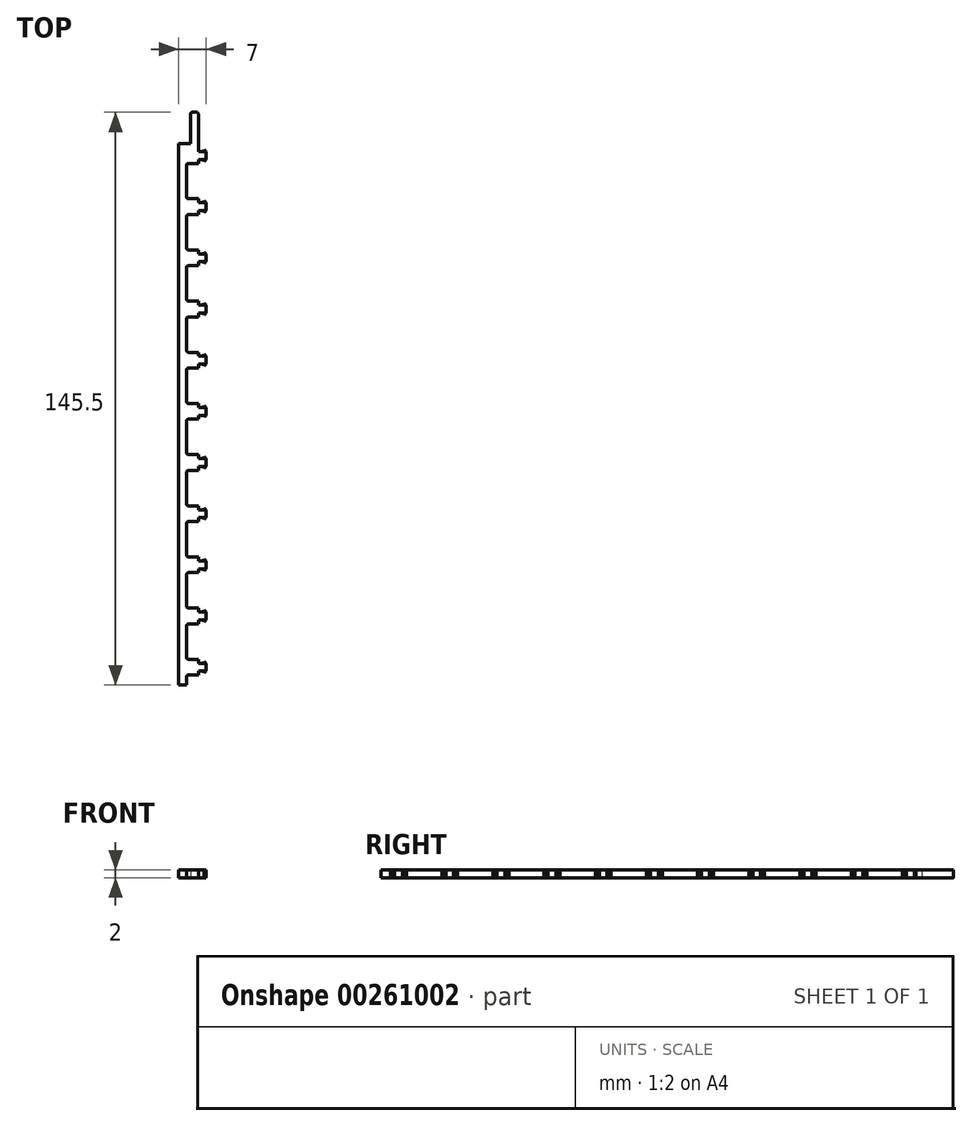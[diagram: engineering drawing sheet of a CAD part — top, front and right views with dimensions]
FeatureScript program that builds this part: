
annotation { "Feature Type Name" : "Feature", "Feature Type Description" : "" }
export const myFeature = defineFeature(function(context is Context, id is Id, definition is map)
    precondition{}
    {
        {
            var Q0;
            Q0=qCreatedBy(makeId("Top.planeOp"),FACE);
            var sketch = newSketch(context, id + "F0", { "sketchPlane" : qUnion([Q0])});
            skLineSegment(sketch, "E0.bottom", {"start": v(-167, 137.5) * mm, "end": v(167, 137.5) * mm});
            skLineSegment(sketch, "E0.top", {"start": v(-167, -137.5) * mm, "end": v(167, -137.5) * mm});
            skLineSegment(sketch, "E0.left", {"start": v(-167, 137.5) * mm, "end": v(-167, -137.5) * mm});
            skLineSegment(sketch, "E0.right", {"start": v(167, 137.5) * mm, "end": v(167, -137.5) * mm});
            skPoint(sketch, "E0.middle", {"position": v(0, 0) * mm});
            skLineSegment(sketch, "E1", {"start": v(-167, 137.5) * mm, "end": v(-172, 137.5) * mm});
            skLineSegment(sketch, "E2", {"start": v(-172, 137.5) * mm, "end": v(-172, -137.5) * mm});
            skLineSegment(sketch, "E3", {"start": v(-172, -137.5) * mm, "end": v(-167, -137.5) * mm});
            skLineSegment(sketch, "E4", {"start": v(-167, 132.5) * mm, "end": v(-169.5, 132.5) * mm});
            skLineSegment(sketch, "E5", {"start": v(-170, 132) * mm, "end": v(-170, 124) * mm});
            skLineSegment(sketch, "E6", {"start": v(-169.5, 123.5) * mm, "end": v(-167, 123.5) * mm});
            skLineSegment(sketch, "E7", {"start": v(-169, 137.5) * mm, "end": v(-169, 145) * mm});
            skLineSegment(sketch, "E8", {"start": v(-168.5, 145.5) * mm, "end": v(-167.5, 145.5) * mm});
            skLineSegment(sketch, "E9", {"start": v(-167, 145) * mm, "end": v(-167, 137.5) * mm});
            skPoint(sketch, "E10.visualSharp", {"position": v(-169, 145.5) * mm});
            skArc(sketch, "E10.filletArc", {"start": v(-168.5, 145.5) * mm, "mid": v(-168.85, 145.35) * mm, "end": v(-169, 145) * mm});
            skPoint(sketch, "E11.visualSharp", {"position": v(-167, 145.5) * mm});
            skArc(sketch, "E11.filletArc", {"start": v(-167, 145) * mm, "mid": v(-167.15, 145.35) * mm, "end": v(-167.5, 145.5) * mm});
            skLineSegment(sketch, "E12", {"start": v(-167, 135.5) * mm, "end": v(-165.5, 135.5) * mm});
            skLineSegment(sketch, "E13", {"start": v(-165.5, 135.5) * mm, "end": v(-165.5, 136) * mm});
            skLineSegment(sketch, "E14", {"start": v(-165.5, 136) * mm, "end": v(-165, 135.5) * mm});
            skLineSegment(sketch, "E15", {"start": v(-167, 134.5) * mm, "end": v(-162.16, 134.5) * mm, "construction": true});
            skLineSegment(sketch, "E16.MirrorCS", {"start": v(-167, 133.5) * mm, "end": v(-165.5, 133.5) * mm});
            skLineSegment(sketch, "E17.MirrorCS", {"start": v(-165.5, 133.5) * mm, "end": v(-165.5, 133) * mm});
            skLineSegment(sketch, "E18.MirrorCS", {"start": v(-165.5, 133) * mm, "end": v(-165, 133.5) * mm});
            skLineSegment(sketch, "E19", {"start": v(-165, 135.5) * mm, "end": v(-165, 133.5) * mm});
            skPoint(sketch, "E20.visualSharp", {"position": v(-170, 132.5) * mm});
            skArc(sketch, "E20.filletArc", {"start": v(-169.5, 132.5) * mm, "mid": v(-169.85, 132.35) * mm, "end": v(-170, 132) * mm});
            skPoint(sketch, "E21.visualSharp", {"position": v(-170, 123.5) * mm});
            skArc(sketch, "E21.filletArc", {"start": v(-170, 124) * mm, "mid": v(-169.85, 123.65) * mm, "end": v(-169.5, 123.5) * mm});
            skLineSegment(sketch, "E22.0.1.0", {"start": v(-167, 120.5) * mm, "end": v(-165.5, 120.5) * mm});
            skLineSegment(sketch, "E22.0.1.1", {"start": v(-165.5, 120.5) * mm, "end": v(-165.5, 120) * mm});
            skLineSegment(sketch, "E22.0.1.2", {"start": v(-165.5, 120) * mm, "end": v(-165, 120.5) * mm});
            skLineSegment(sketch, "E22.0.1.3", {"start": v(-165, 122.5) * mm, "end": v(-165, 120.5) * mm});
            skLineSegment(sketch, "E22.0.1.4", {"start": v(-165.5, 123) * mm, "end": v(-165, 122.5) * mm});
            skLineSegment(sketch, "E22.0.1.5", {"start": v(-165.5, 122.5) * mm, "end": v(-165.5, 123) * mm});
            skLineSegment(sketch, "E22.0.1.6", {"start": v(-167, 122.5) * mm, "end": v(-165.5, 122.5) * mm});
            skLineSegment(sketch, "E22.0.1.7", {"start": v(-167, 119.5) * mm, "end": v(-169.5, 119.5) * mm});
            skArc(sketch, "E22.0.1.8", {"start": v(-169.5, 119.5) * mm, "mid": v(-169.85, 119.35) * mm, "end": v(-170, 119) * mm});
            skLineSegment(sketch, "E22.0.1.9", {"start": v(-170, 119) * mm, "end": v(-170, 111) * mm});
            skArc(sketch, "E22.0.1.10", {"start": v(-170, 111) * mm, "mid": v(-169.85, 110.65) * mm, "end": v(-169.5, 110.5) * mm});
            skLineSegment(sketch, "E22.0.1.11", {"start": v(-169.5, 110.5) * mm, "end": v(-167, 110.5) * mm});
            skLineSegment(sketch, "E22.0.2.0", {"start": v(-167, 107.5) * mm, "end": v(-165.5, 107.5) * mm});
            skLineSegment(sketch, "E22.0.2.1", {"start": v(-165.5, 107.5) * mm, "end": v(-165.5, 107) * mm});
            skLineSegment(sketch, "E22.0.2.2", {"start": v(-165.5, 107) * mm, "end": v(-165, 107.5) * mm});
            skLineSegment(sketch, "E22.0.2.3", {"start": v(-165, 109.5) * mm, "end": v(-165, 107.5) * mm});
            skLineSegment(sketch, "E22.0.2.4", {"start": v(-165.5, 110) * mm, "end": v(-165, 109.5) * mm});
            skLineSegment(sketch, "E22.0.2.5", {"start": v(-165.5, 109.5) * mm, "end": v(-165.5, 110) * mm});
            skLineSegment(sketch, "E22.0.2.6", {"start": v(-167, 109.5) * mm, "end": v(-165.5, 109.5) * mm});
            skLineSegment(sketch, "E22.0.2.7", {"start": v(-167, 106.5) * mm, "end": v(-169.5, 106.5) * mm});
            skArc(sketch, "E22.0.2.8", {"start": v(-169.5, 106.5) * mm, "mid": v(-169.85, 106.35) * mm, "end": v(-170, 106) * mm});
            skLineSegment(sketch, "E22.0.2.9", {"start": v(-170, 106) * mm, "end": v(-170, 98) * mm});
            skArc(sketch, "E22.0.2.10", {"start": v(-170, 98) * mm, "mid": v(-169.85, 97.65) * mm, "end": v(-169.5, 97.5) * mm});
            skLineSegment(sketch, "E22.0.2.11", {"start": v(-169.5, 97.5) * mm, "end": v(-167, 97.5) * mm});
            skLineSegment(sketch, "E22.0.3.0", {"start": v(-167, 94.5) * mm, "end": v(-165.5, 94.5) * mm});
            skLineSegment(sketch, "E22.0.3.1", {"start": v(-165.5, 94.5) * mm, "end": v(-165.5, 94) * mm});
            skLineSegment(sketch, "E22.0.3.2", {"start": v(-165.5, 94) * mm, "end": v(-165, 94.5) * mm});
            skLineSegment(sketch, "E22.0.3.3", {"start": v(-165, 96.5) * mm, "end": v(-165, 94.5) * mm});
            skLineSegment(sketch, "E22.0.3.4", {"start": v(-165.5, 97) * mm, "end": v(-165, 96.5) * mm});
            skLineSegment(sketch, "E22.0.3.5", {"start": v(-165.5, 96.5) * mm, "end": v(-165.5, 97) * mm});
            skLineSegment(sketch, "E22.0.3.6", {"start": v(-167, 96.5) * mm, "end": v(-165.5, 96.5) * mm});
            skLineSegment(sketch, "E22.0.3.7", {"start": v(-167, 93.5) * mm, "end": v(-169.5, 93.5) * mm});
            skArc(sketch, "E22.0.3.8", {"start": v(-169.5, 93.5) * mm, "mid": v(-169.85, 93.35) * mm, "end": v(-170, 93) * mm});
            skLineSegment(sketch, "E22.0.3.9", {"start": v(-170, 93) * mm, "end": v(-170, 85) * mm});
            skArc(sketch, "E22.0.3.10", {"start": v(-170, 85) * mm, "mid": v(-169.85, 84.65) * mm, "end": v(-169.5, 84.5) * mm});
            skLineSegment(sketch, "E22.0.3.11", {"start": v(-169.5, 84.5) * mm, "end": v(-167, 84.5) * mm});
            skLineSegment(sketch, "E22.0.4.0", {"start": v(-167, 81.5) * mm, "end": v(-165.5, 81.5) * mm});
            skLineSegment(sketch, "E22.0.4.1", {"start": v(-165.5, 81.5) * mm, "end": v(-165.5, 81) * mm});
            skLineSegment(sketch, "E22.0.4.2", {"start": v(-165.5, 81) * mm, "end": v(-165, 81.5) * mm});
            skLineSegment(sketch, "E22.0.4.3", {"start": v(-165, 83.5) * mm, "end": v(-165, 81.5) * mm});
            skLineSegment(sketch, "E22.0.4.4", {"start": v(-165.5, 84) * mm, "end": v(-165, 83.5) * mm});
            skLineSegment(sketch, "E22.0.4.5", {"start": v(-165.5, 83.5) * mm, "end": v(-165.5, 84) * mm});
            skLineSegment(sketch, "E22.0.4.6", {"start": v(-167, 83.5) * mm, "end": v(-165.5, 83.5) * mm});
            skLineSegment(sketch, "E22.0.4.7", {"start": v(-167, 80.5) * mm, "end": v(-169.5, 80.5) * mm});
            skArc(sketch, "E22.0.4.8", {"start": v(-169.5, 80.5) * mm, "mid": v(-169.85, 80.35) * mm, "end": v(-170, 80) * mm});
            skLineSegment(sketch, "E22.0.4.9", {"start": v(-170, 80) * mm, "end": v(-170, 72) * mm});
            skArc(sketch, "E22.0.4.10", {"start": v(-170, 72) * mm, "mid": v(-169.85, 71.65) * mm, "end": v(-169.5, 71.5) * mm});
            skLineSegment(sketch, "E22.0.4.11", {"start": v(-169.5, 71.5) * mm, "end": v(-167, 71.5) * mm});
            skLineSegment(sketch, "E22.0.5.0", {"start": v(-167, 68.5) * mm, "end": v(-165.5, 68.5) * mm});
            skLineSegment(sketch, "E22.0.5.1", {"start": v(-165.5, 68.5) * mm, "end": v(-165.5, 68) * mm});
            skLineSegment(sketch, "E22.0.5.2", {"start": v(-165.5, 68) * mm, "end": v(-165, 68.5) * mm});
            skLineSegment(sketch, "E22.0.5.3", {"start": v(-165, 70.5) * mm, "end": v(-165, 68.5) * mm});
            skLineSegment(sketch, "E22.0.5.4", {"start": v(-165.5, 71) * mm, "end": v(-165, 70.5) * mm});
            skLineSegment(sketch, "E22.0.5.5", {"start": v(-165.5, 70.5) * mm, "end": v(-165.5, 71) * mm});
            skLineSegment(sketch, "E22.0.5.6", {"start": v(-167, 70.5) * mm, "end": v(-165.5, 70.5) * mm});
            skLineSegment(sketch, "E22.0.5.7", {"start": v(-167, 67.5) * mm, "end": v(-169.5, 67.5) * mm});
            skArc(sketch, "E22.0.5.8", {"start": v(-169.5, 67.5) * mm, "mid": v(-169.85, 67.35) * mm, "end": v(-170, 67) * mm});
            skLineSegment(sketch, "E22.0.5.9", {"start": v(-170, 67) * mm, "end": v(-170, 59) * mm});
            skArc(sketch, "E22.0.5.10", {"start": v(-170, 59) * mm, "mid": v(-169.85, 58.65) * mm, "end": v(-169.5, 58.5) * mm});
            skLineSegment(sketch, "E22.0.5.11", {"start": v(-169.5, 58.5) * mm, "end": v(-167, 58.5) * mm});
            skLineSegment(sketch, "E22.0.6.0", {"start": v(-167, 55.5) * mm, "end": v(-165.5, 55.5) * mm});
            skLineSegment(sketch, "E22.0.6.1", {"start": v(-165.5, 55.5) * mm, "end": v(-165.5, 55) * mm});
            skLineSegment(sketch, "E22.0.6.2", {"start": v(-165.5, 55) * mm, "end": v(-165, 55.5) * mm});
            skLineSegment(sketch, "E22.0.6.3", {"start": v(-165, 57.5) * mm, "end": v(-165, 55.5) * mm});
            skLineSegment(sketch, "E22.0.6.4", {"start": v(-165.5, 58) * mm, "end": v(-165, 57.5) * mm});
            skLineSegment(sketch, "E22.0.6.5", {"start": v(-165.5, 57.5) * mm, "end": v(-165.5, 58) * mm});
            skLineSegment(sketch, "E22.0.6.6", {"start": v(-167, 57.5) * mm, "end": v(-165.5, 57.5) * mm});
            skLineSegment(sketch, "E22.0.6.7", {"start": v(-167, 54.5) * mm, "end": v(-169.5, 54.5) * mm});
            skArc(sketch, "E22.0.6.8", {"start": v(-169.5, 54.5) * mm, "mid": v(-169.85, 54.35) * mm, "end": v(-170, 54) * mm});
            skLineSegment(sketch, "E22.0.6.9", {"start": v(-170, 54) * mm, "end": v(-170, 46) * mm});
            skArc(sketch, "E22.0.6.10", {"start": v(-170, 46) * mm, "mid": v(-169.85, 45.65) * mm, "end": v(-169.5, 45.5) * mm});
            skLineSegment(sketch, "E22.0.6.11", {"start": v(-169.5, 45.5) * mm, "end": v(-167, 45.5) * mm});
            skLineSegment(sketch, "E22.0.7.0", {"start": v(-167, 42.5) * mm, "end": v(-165.5, 42.5) * mm});
            skLineSegment(sketch, "E22.0.7.1", {"start": v(-165.5, 42.5) * mm, "end": v(-165.5, 42) * mm});
            skLineSegment(sketch, "E22.0.7.2", {"start": v(-165.5, 42) * mm, "end": v(-165, 42.5) * mm});
            skLineSegment(sketch, "E22.0.7.3", {"start": v(-165, 44.5) * mm, "end": v(-165, 42.5) * mm});
            skLineSegment(sketch, "E22.0.7.4", {"start": v(-165.5, 45) * mm, "end": v(-165, 44.5) * mm});
            skLineSegment(sketch, "E22.0.7.5", {"start": v(-165.5, 44.5) * mm, "end": v(-165.5, 45) * mm});
            skLineSegment(sketch, "E22.0.7.6", {"start": v(-167, 44.5) * mm, "end": v(-165.5, 44.5) * mm});
            skLineSegment(sketch, "E22.0.7.7", {"start": v(-167, 41.5) * mm, "end": v(-169.5, 41.5) * mm});
            skArc(sketch, "E22.0.7.8", {"start": v(-169.5, 41.5) * mm, "mid": v(-169.85, 41.35) * mm, "end": v(-170, 41) * mm});
            skLineSegment(sketch, "E22.0.7.9", {"start": v(-170, 41) * mm, "end": v(-170, 33) * mm});
            skArc(sketch, "E22.0.7.10", {"start": v(-170, 33) * mm, "mid": v(-169.85, 32.65) * mm, "end": v(-169.5, 32.5) * mm});
            skLineSegment(sketch, "E22.0.7.11", {"start": v(-169.5, 32.5) * mm, "end": v(-167, 32.5) * mm});
            skLineSegment(sketch, "E22.0.8.0", {"start": v(-167, 29.5) * mm, "end": v(-165.5, 29.5) * mm});
            skLineSegment(sketch, "E22.0.8.1", {"start": v(-165.5, 29.5) * mm, "end": v(-165.5, 29) * mm});
            skLineSegment(sketch, "E22.0.8.2", {"start": v(-165.5, 29) * mm, "end": v(-165, 29.5) * mm});
            skLineSegment(sketch, "E22.0.8.3", {"start": v(-165, 31.5) * mm, "end": v(-165, 29.5) * mm});
            skLineSegment(sketch, "E22.0.8.4", {"start": v(-165.5, 32) * mm, "end": v(-165, 31.5) * mm});
            skLineSegment(sketch, "E22.0.8.5", {"start": v(-165.5, 31.5) * mm, "end": v(-165.5, 32) * mm});
            skLineSegment(sketch, "E22.0.8.6", {"start": v(-167, 31.5) * mm, "end": v(-165.5, 31.5) * mm});
            skLineSegment(sketch, "E22.0.8.7", {"start": v(-167, 28.5) * mm, "end": v(-169.5, 28.5) * mm});
            skArc(sketch, "E22.0.8.8", {"start": v(-169.5, 28.5) * mm, "mid": v(-169.85, 28.35) * mm, "end": v(-170, 28) * mm});
            skLineSegment(sketch, "E22.0.8.9", {"start": v(-170, 28) * mm, "end": v(-170, 20) * mm});
            skArc(sketch, "E22.0.8.10", {"start": v(-170, 20) * mm, "mid": v(-169.85, 19.65) * mm, "end": v(-169.5, 19.5) * mm});
            skLineSegment(sketch, "E22.0.8.11", {"start": v(-169.5, 19.5) * mm, "end": v(-167, 19.5) * mm});
            skLineSegment(sketch, "E22.0.9.0", {"start": v(-167, 16.5) * mm, "end": v(-165.5, 16.5) * mm});
            skLineSegment(sketch, "E22.0.9.1", {"start": v(-165.5, 16.5) * mm, "end": v(-165.5, 16) * mm});
            skLineSegment(sketch, "E22.0.9.2", {"start": v(-165.5, 16) * mm, "end": v(-165, 16.5) * mm});
            skLineSegment(sketch, "E22.0.9.3", {"start": v(-165, 18.5) * mm, "end": v(-165, 16.5) * mm});
            skLineSegment(sketch, "E22.0.9.4", {"start": v(-165.5, 19) * mm, "end": v(-165, 18.5) * mm});
            skLineSegment(sketch, "E22.0.9.5", {"start": v(-165.5, 18.5) * mm, "end": v(-165.5, 19) * mm});
            skLineSegment(sketch, "E22.0.9.6", {"start": v(-167, 18.5) * mm, "end": v(-165.5, 18.5) * mm});
            skLineSegment(sketch, "E22.0.9.7", {"start": v(-167, 15.5) * mm, "end": v(-169.5, 15.5) * mm});
            skArc(sketch, "E22.0.9.8", {"start": v(-169.5, 15.5) * mm, "mid": v(-169.85, 15.35) * mm, "end": v(-170, 15) * mm});
            skLineSegment(sketch, "E22.0.9.9", {"start": v(-170, 15) * mm, "end": v(-170, 7) * mm});
            skArc(sketch, "E22.0.9.10", {"start": v(-170, 7) * mm, "mid": v(-169.85, 6.65) * mm, "end": v(-169.5, 6.5) * mm});
            skLineSegment(sketch, "E22.0.9.11", {"start": v(-169.5, 6.5) * mm, "end": v(-167, 6.5) * mm});
            skLineSegment(sketch, "E22.0.10.0", {"start": v(-167, 3.5) * mm, "end": v(-165.5, 3.5) * mm});
            skLineSegment(sketch, "E22.0.10.1", {"start": v(-165.5, 3.5) * mm, "end": v(-165.5, 3) * mm});
            skLineSegment(sketch, "E22.0.10.2", {"start": v(-165.5, 3) * mm, "end": v(-165, 3.5) * mm});
            skLineSegment(sketch, "E22.0.10.3", {"start": v(-165, 5.5) * mm, "end": v(-165, 3.5) * mm});
            skLineSegment(sketch, "E22.0.10.4", {"start": v(-165.5, 6) * mm, "end": v(-165, 5.5) * mm});
            skLineSegment(sketch, "E22.0.10.5", {"start": v(-165.5, 5.5) * mm, "end": v(-165.5, 6) * mm});
            skLineSegment(sketch, "E22.0.10.6", {"start": v(-167, 5.5) * mm, "end": v(-165.5, 5.5) * mm});
            skLineSegment(sketch, "E22.0.10.7", {"start": v(-167, 2.5) * mm, "end": v(-169.5, 2.5) * mm});
            skArc(sketch, "E22.0.10.8", {"start": v(-169.5, 2.5) * mm, "mid": v(-169.85, 2.35) * mm, "end": v(-170, 2) * mm});
            skLineSegment(sketch, "E22.0.10.9", {"start": v(-170, 2) * mm, "end": v(-170, -6) * mm});
            skArc(sketch, "E22.0.10.10", {"start": v(-170, -6) * mm, "mid": v(-169.85, -6.35) * mm, "end": v(-169.5, -6.5) * mm});
            skLineSegment(sketch, "E22.0.10.11", {"start": v(-169.5, -6.5) * mm, "end": v(-167, -6.5) * mm});
            skLineSegment(sketch, "E22.0.11.0", {"start": v(-167, -9.5) * mm, "end": v(-165.5, -9.5) * mm});
            skLineSegment(sketch, "E22.0.11.1", {"start": v(-165.5, -9.5) * mm, "end": v(-165.5, -10) * mm});
            skLineSegment(sketch, "E22.0.11.2", {"start": v(-165.5, -10) * mm, "end": v(-165, -9.5) * mm});
            skLineSegment(sketch, "E22.0.11.3", {"start": v(-165, -7.5) * mm, "end": v(-165, -9.5) * mm});
            skLineSegment(sketch, "E22.0.11.4", {"start": v(-165.5, -7) * mm, "end": v(-165, -7.5) * mm});
            skLineSegment(sketch, "E22.0.11.5", {"start": v(-165.5, -7.5) * mm, "end": v(-165.5, -7) * mm});
            skLineSegment(sketch, "E22.0.11.6", {"start": v(-167, -7.5) * mm, "end": v(-165.5, -7.5) * mm});
            skLineSegment(sketch, "E22.0.11.7", {"start": v(-167, -10.5) * mm, "end": v(-169.5, -10.5) * mm});
            skArc(sketch, "E22.0.11.8", {"start": v(-169.5, -10.5) * mm, "mid": v(-169.85, -10.65) * mm, "end": v(-170, -11) * mm});
            skLineSegment(sketch, "E22.0.11.9", {"start": v(-170, -11) * mm, "end": v(-170, -19) * mm});
            skArc(sketch, "E22.0.11.10", {"start": v(-170, -19) * mm, "mid": v(-169.85, -19.35) * mm, "end": v(-169.5, -19.5) * mm});
            skLineSegment(sketch, "E22.0.11.11", {"start": v(-169.5, -19.5) * mm, "end": v(-167, -19.5) * mm});
            skLineSegment(sketch, "E22.0.12.0", {"start": v(-167, -22.5) * mm, "end": v(-165.5, -22.5) * mm});
            skLineSegment(sketch, "E22.0.12.1", {"start": v(-165.5, -22.5) * mm, "end": v(-165.5, -23) * mm});
            skLineSegment(sketch, "E22.0.12.2", {"start": v(-165.5, -23) * mm, "end": v(-165, -22.5) * mm});
            skLineSegment(sketch, "E22.0.12.3", {"start": v(-165, -20.5) * mm, "end": v(-165, -22.5) * mm});
            skLineSegment(sketch, "E22.0.12.4", {"start": v(-165.5, -20) * mm, "end": v(-165, -20.5) * mm});
            skLineSegment(sketch, "E22.0.12.5", {"start": v(-165.5, -20.5) * mm, "end": v(-165.5, -20) * mm});
            skLineSegment(sketch, "E22.0.12.6", {"start": v(-167, -20.5) * mm, "end": v(-165.5, -20.5) * mm});
            skLineSegment(sketch, "E22.0.12.7", {"start": v(-167, -23.5) * mm, "end": v(-169.5, -23.5) * mm});
            skArc(sketch, "E22.0.12.8", {"start": v(-169.5, -23.5) * mm, "mid": v(-169.85, -23.65) * mm, "end": v(-170, -24) * mm});
            skLineSegment(sketch, "E22.0.12.9", {"start": v(-170, -24) * mm, "end": v(-170, -32) * mm});
            skArc(sketch, "E22.0.12.10", {"start": v(-170, -32) * mm, "mid": v(-169.85, -32.35) * mm, "end": v(-169.5, -32.5) * mm});
            skLineSegment(sketch, "E22.0.12.11", {"start": v(-169.5, -32.5) * mm, "end": v(-167, -32.5) * mm});
            skLineSegment(sketch, "E22.0.13.0", {"start": v(-167, -35.5) * mm, "end": v(-165.5, -35.5) * mm});
            skLineSegment(sketch, "E22.0.13.1", {"start": v(-165.5, -35.5) * mm, "end": v(-165.5, -36) * mm});
            skLineSegment(sketch, "E22.0.13.2", {"start": v(-165.5, -36) * mm, "end": v(-165, -35.5) * mm});
            skLineSegment(sketch, "E22.0.13.3", {"start": v(-165, -33.5) * mm, "end": v(-165, -35.5) * mm});
            skLineSegment(sketch, "E22.0.13.4", {"start": v(-165.5, -33) * mm, "end": v(-165, -33.5) * mm});
            skLineSegment(sketch, "E22.0.13.5", {"start": v(-165.5, -33.5) * mm, "end": v(-165.5, -33) * mm});
            skLineSegment(sketch, "E22.0.13.6", {"start": v(-167, -33.5) * mm, "end": v(-165.5, -33.5) * mm});
            skLineSegment(sketch, "E22.0.13.7", {"start": v(-167, -36.5) * mm, "end": v(-169.5, -36.5) * mm});
            skArc(sketch, "E22.0.13.8", {"start": v(-169.5, -36.5) * mm, "mid": v(-169.85, -36.65) * mm, "end": v(-170, -37) * mm});
            skLineSegment(sketch, "E22.0.13.9", {"start": v(-170, -37) * mm, "end": v(-170, -45) * mm});
            skArc(sketch, "E22.0.13.10", {"start": v(-170, -45) * mm, "mid": v(-169.85, -45.35) * mm, "end": v(-169.5, -45.5) * mm});
            skLineSegment(sketch, "E22.0.13.11", {"start": v(-169.5, -45.5) * mm, "end": v(-167, -45.5) * mm});
            skLineSegment(sketch, "E22.0.14.0", {"start": v(-167, -48.5) * mm, "end": v(-165.5, -48.5) * mm});
            skLineSegment(sketch, "E22.0.14.1", {"start": v(-165.5, -48.5) * mm, "end": v(-165.5, -49) * mm});
            skLineSegment(sketch, "E22.0.14.2", {"start": v(-165.5, -49) * mm, "end": v(-165, -48.5) * mm});
            skLineSegment(sketch, "E22.0.14.3", {"start": v(-165, -46.5) * mm, "end": v(-165, -48.5) * mm});
            skLineSegment(sketch, "E22.0.14.4", {"start": v(-165.5, -46) * mm, "end": v(-165, -46.5) * mm});
            skLineSegment(sketch, "E22.0.14.5", {"start": v(-165.5, -46.5) * mm, "end": v(-165.5, -46) * mm});
            skLineSegment(sketch, "E22.0.14.6", {"start": v(-167, -46.5) * mm, "end": v(-165.5, -46.5) * mm});
            skLineSegment(sketch, "E22.0.14.7", {"start": v(-167, -49.5) * mm, "end": v(-169.5, -49.5) * mm});
            skArc(sketch, "E22.0.14.8", {"start": v(-169.5, -49.5) * mm, "mid": v(-169.85, -49.65) * mm, "end": v(-170, -50) * mm});
            skLineSegment(sketch, "E22.0.14.9", {"start": v(-170, -50) * mm, "end": v(-170, -58) * mm});
            skArc(sketch, "E22.0.14.10", {"start": v(-170, -58) * mm, "mid": v(-169.85, -58.35) * mm, "end": v(-169.5, -58.5) * mm});
            skLineSegment(sketch, "E22.0.14.11", {"start": v(-169.5, -58.5) * mm, "end": v(-167, -58.5) * mm});
            skLineSegment(sketch, "E22.0.15.0", {"start": v(-167, -61.5) * mm, "end": v(-165.5, -61.5) * mm});
            skLineSegment(sketch, "E22.0.15.1", {"start": v(-165.5, -61.5) * mm, "end": v(-165.5, -62) * mm});
            skLineSegment(sketch, "E22.0.15.2", {"start": v(-165.5, -62) * mm, "end": v(-165, -61.5) * mm});
            skLineSegment(sketch, "E22.0.15.3", {"start": v(-165, -59.5) * mm, "end": v(-165, -61.5) * mm});
            skLineSegment(sketch, "E22.0.15.4", {"start": v(-165.5, -59) * mm, "end": v(-165, -59.5) * mm});
            skLineSegment(sketch, "E22.0.15.5", {"start": v(-165.5, -59.5) * mm, "end": v(-165.5, -59) * mm});
            skLineSegment(sketch, "E22.0.15.6", {"start": v(-167, -59.5) * mm, "end": v(-165.5, -59.5) * mm});
            skLineSegment(sketch, "E22.0.15.7", {"start": v(-167, -62.5) * mm, "end": v(-169.5, -62.5) * mm});
            skArc(sketch, "E22.0.15.8", {"start": v(-169.5, -62.5) * mm, "mid": v(-169.85, -62.65) * mm, "end": v(-170, -63) * mm});
            skLineSegment(sketch, "E22.0.15.9", {"start": v(-170, -63) * mm, "end": v(-170, -71) * mm});
            skArc(sketch, "E22.0.15.10", {"start": v(-170, -71) * mm, "mid": v(-169.85, -71.35) * mm, "end": v(-169.5, -71.5) * mm});
            skLineSegment(sketch, "E22.0.15.11", {"start": v(-169.5, -71.5) * mm, "end": v(-167, -71.5) * mm});
            skLineSegment(sketch, "E22.0.16.0", {"start": v(-167, -74.5) * mm, "end": v(-165.5, -74.5) * mm});
            skLineSegment(sketch, "E22.0.16.1", {"start": v(-165.5, -74.5) * mm, "end": v(-165.5, -75) * mm});
            skLineSegment(sketch, "E22.0.16.2", {"start": v(-165.5, -75) * mm, "end": v(-165, -74.5) * mm});
            skLineSegment(sketch, "E22.0.16.3", {"start": v(-165, -72.5) * mm, "end": v(-165, -74.5) * mm});
            skLineSegment(sketch, "E22.0.16.4", {"start": v(-165.5, -72) * mm, "end": v(-165, -72.5) * mm});
            skLineSegment(sketch, "E22.0.16.5", {"start": v(-165.5, -72.5) * mm, "end": v(-165.5, -72) * mm});
            skLineSegment(sketch, "E22.0.16.6", {"start": v(-167, -72.5) * mm, "end": v(-165.5, -72.5) * mm});
            skLineSegment(sketch, "E22.0.16.7", {"start": v(-167, -75.5) * mm, "end": v(-169.5, -75.5) * mm});
            skArc(sketch, "E22.0.16.8", {"start": v(-169.5, -75.5) * mm, "mid": v(-169.85, -75.65) * mm, "end": v(-170, -76) * mm});
            skLineSegment(sketch, "E22.0.16.9", {"start": v(-170, -76) * mm, "end": v(-170, -84) * mm});
            skArc(sketch, "E22.0.16.10", {"start": v(-170, -84) * mm, "mid": v(-169.85, -84.35) * mm, "end": v(-169.5, -84.5) * mm});
            skLineSegment(sketch, "E22.0.16.11", {"start": v(-169.5, -84.5) * mm, "end": v(-167, -84.5) * mm});
            skLineSegment(sketch, "E22.0.17.0", {"start": v(-167, -87.5) * mm, "end": v(-165.5, -87.5) * mm});
            skLineSegment(sketch, "E22.0.17.1", {"start": v(-165.5, -87.5) * mm, "end": v(-165.5, -88) * mm});
            skLineSegment(sketch, "E22.0.17.2", {"start": v(-165.5, -88) * mm, "end": v(-165, -87.5) * mm});
            skLineSegment(sketch, "E22.0.17.3", {"start": v(-165, -85.5) * mm, "end": v(-165, -87.5) * mm});
            skLineSegment(sketch, "E22.0.17.4", {"start": v(-165.5, -85) * mm, "end": v(-165, -85.5) * mm});
            skLineSegment(sketch, "E22.0.17.5", {"start": v(-165.5, -85.5) * mm, "end": v(-165.5, -85) * mm});
            skLineSegment(sketch, "E22.0.17.6", {"start": v(-167, -85.5) * mm, "end": v(-165.5, -85.5) * mm});
            skLineSegment(sketch, "E22.0.17.7", {"start": v(-167, -88.5) * mm, "end": v(-169.5, -88.5) * mm});
            skArc(sketch, "E22.0.17.8", {"start": v(-169.5, -88.5) * mm, "mid": v(-169.85, -88.65) * mm, "end": v(-170, -89) * mm});
            skLineSegment(sketch, "E22.0.17.9", {"start": v(-170, -89) * mm, "end": v(-170, -97) * mm});
            skArc(sketch, "E22.0.17.10", {"start": v(-170, -97) * mm, "mid": v(-169.85, -97.35) * mm, "end": v(-169.5, -97.5) * mm});
            skLineSegment(sketch, "E22.0.17.11", {"start": v(-169.5, -97.5) * mm, "end": v(-167, -97.5) * mm});
            skLineSegment(sketch, "E22.0.18.0", {"start": v(-167, -100.5) * mm, "end": v(-165.5, -100.5) * mm});
            skLineSegment(sketch, "E22.0.18.1", {"start": v(-165.5, -100.5) * mm, "end": v(-165.5, -101) * mm});
            skLineSegment(sketch, "E22.0.18.2", {"start": v(-165.5, -101) * mm, "end": v(-165, -100.5) * mm});
            skLineSegment(sketch, "E22.0.18.3", {"start": v(-165, -98.5) * mm, "end": v(-165, -100.5) * mm});
            skLineSegment(sketch, "E22.0.18.4", {"start": v(-165.5, -98) * mm, "end": v(-165, -98.5) * mm});
            skLineSegment(sketch, "E22.0.18.5", {"start": v(-165.5, -98.5) * mm, "end": v(-165.5, -98) * mm});
            skLineSegment(sketch, "E22.0.18.6", {"start": v(-167, -98.5) * mm, "end": v(-165.5, -98.5) * mm});
            skLineSegment(sketch, "E22.0.18.7", {"start": v(-167, -101.5) * mm, "end": v(-169.5, -101.5) * mm});
            skArc(sketch, "E22.0.18.8", {"start": v(-169.5, -101.5) * mm, "mid": v(-169.85, -101.65) * mm, "end": v(-170, -102) * mm});
            skLineSegment(sketch, "E22.0.18.9", {"start": v(-170, -102) * mm, "end": v(-170, -110) * mm});
            skArc(sketch, "E22.0.18.10", {"start": v(-170, -110) * mm, "mid": v(-169.85, -110.35) * mm, "end": v(-169.5, -110.5) * mm});
            skLineSegment(sketch, "E22.0.18.11", {"start": v(-169.5, -110.5) * mm, "end": v(-167, -110.5) * mm});
            skLineSegment(sketch, "E22.direction1", {"start": v(-169.5, 123.5) * mm, "end": v(-144.5, 123.5) * mm, "construction": true});
            skLineSegment(sketch, "E22.direction2", {"start": v(-169.5, 123.5) * mm, "end": v(-169.5, 110.5) * mm, "construction": true});
            skLineSegment(sketch, "E23", {"start": v(-170, -106) * mm, "end": v(-159.1, -106) * mm, "construction": true});
            skLineSegment(sketch, "E24.MirrorCS", {"start": v(-167, -111.5) * mm, "end": v(-165.5, -111.5) * mm});
            skLineSegment(sketch, "E25.MirrorCS", {"start": v(-165.5, -111.5) * mm, "end": v(-165.5, -111) * mm});
            skLineSegment(sketch, "E26.MirrorCS", {"start": v(-165.5, -111) * mm, "end": v(-165, -111.5) * mm});
            skLineSegment(sketch, "E27.MirrorCS", {"start": v(-165, -113.5) * mm, "end": v(-165, -111.5) * mm});
            skLineSegment(sketch, "E28.MirrorCS", {"start": v(-165.5, -114) * mm, "end": v(-165, -113.5) * mm});
            skLineSegment(sketch, "E29.MirrorCS", {"start": v(-165.5, -113.5) * mm, "end": v(-165.5, -114) * mm});
            skLineSegment(sketch, "E30.MirrorCS", {"start": v(-167, -113.5) * mm, "end": v(-165.5, -113.5) * mm});
            skLineSegment(sketch, "E31.9.0.19", {"start": v(-165, -111.5) * mm, "end": v(-165, -113.5) * mm});
            skLineSegment(sketch, "E31.21.0.19", {"start": v(-167, -114.5) * mm, "end": v(-169.5, -114.5) * mm});
            skArc(sketch, "E31.24.0.19", {"start": v(-169.5, -114.5) * mm, "mid": v(-169.85, -114.65) * mm, "end": v(-170, -115) * mm});
            skLineSegment(sketch, "E31.28.0.19", {"start": v(-170, -115) * mm, "end": v(-170, -123) * mm});
            skArc(sketch, "E31.31.0.19", {"start": v(-170, -123) * mm, "mid": v(-169.85, -123.35) * mm, "end": v(-169.5, -123.5) * mm});
            skLineSegment(sketch, "E31.35.0.19", {"start": v(-169.5, -123.5) * mm, "end": v(-167, -123.5) * mm});
            skLineSegment(sketch, "E31.0.0.20", {"start": v(-167, -126.5) * mm, "end": v(-165.5, -126.5) * mm});
            skLineSegment(sketch, "E31.3.0.20", {"start": v(-165.5, -126.5) * mm, "end": v(-165.5, -127) * mm});
            skLineSegment(sketch, "E31.6.0.20", {"start": v(-165.5, -127) * mm, "end": v(-165, -126.5) * mm});
            skLineSegment(sketch, "E31.9.0.20", {"start": v(-165, -124.5) * mm, "end": v(-165, -126.5) * mm});
            skLineSegment(sketch, "E31.12.0.20", {"start": v(-165.5, -124) * mm, "end": v(-165, -124.5) * mm});
            skLineSegment(sketch, "E31.15.0.20", {"start": v(-165.5, -124.5) * mm, "end": v(-165.5, -124) * mm});
            skLineSegment(sketch, "E31.18.0.20", {"start": v(-167, -124.5) * mm, "end": v(-165.5, -124.5) * mm});
            skLineSegment(sketch, "E31.21.0.20", {"start": v(-167, -127.5) * mm, "end": v(-169.5, -127.5) * mm});
            skArc(sketch, "E31.24.0.20", {"start": v(-169.5, -127.5) * mm, "mid": v(-169.85, -127.65) * mm, "end": v(-170, -128) * mm});
            skLineSegment(sketch, "E31.28.0.20", {"start": v(-170, -128) * mm, "end": v(-170, -136) * mm});
            skArc(sketch, "E31.31.0.20", {"start": v(-170, -136) * mm, "mid": v(-169.85, -136.35) * mm, "end": v(-169.5, -136.5) * mm});
            skLineSegment(sketch, "E31.35.0.20", {"start": v(-169.5, -136.5) * mm, "end": v(-167, -136.5) * mm});
            skLineSegment(sketch, "E32", {"start": v(0, 0) * mm, "end": v(-272.66, 0) * mm, "construction": true});
            skLineSegment(sketch, "E33.MirrorCS", {"start": v(-169, -137.5) * mm, "end": v(-169, -145) * mm});
            skLineSegment(sketch, "E34.MirrorCS", {"start": v(-167, -145) * mm, "end": v(-167, -137.5) * mm});
            skLineSegment(sketch, "E35.MirrorCS", {"start": v(-168.5, -145.5) * mm, "end": v(-167.5, -145.5) * mm});
            skArc(sketch, "E36.MirrorCS", {"start": v(-168.5, -145.5) * mm, "mid": v(-168.85, -145.35) * mm, "end": v(-169, -145) * mm});
            skArc(sketch, "E37.MirrorCS", {"start": v(-167, -145) * mm, "mid": v(-167.15, -145.35) * mm, "end": v(-167.5, -145.5) * mm});
            skLineSegment(sketch, "E38", {"start": v(-170, 0) * mm, "end": v(-172, 0) * mm});
            skSolve(sketch);
        }
        {
            var Q0;
            {var subQ3=sQuery(id+"F0.wireOp",EDGE,"E4");Q0=makeQuery(id+"F0.imprint","IMPRINT",FACE,{"disambiguationData":[TD([[makeQuery(id+"F0.imprint","IMPRINT",EDGE,{"derivedFrom":subQ3}),-1.0]])]});}
            var Q1;
            {var subQ0=sQuery(id+"F0.wireOp",EDGE,"E22.0.10.0");Q1=makeQuery(id+"F0.imprint","IMPRINT",FACE,{"disambiguationData":[TD([[makeQuery(id+"F0.imprint","IMPRINT",EDGE,{"derivedFrom":subQ0}),1.0]])]});}
            var Q2;
            {var subQ0=sQuery(id+"F0.wireOp",EDGE,"E22.0.9.0");Q2=makeQuery(id+"F0.imprint","IMPRINT",FACE,{"disambiguationData":[TD([[makeQuery(id+"F0.imprint","IMPRINT",EDGE,{"derivedFrom":subQ0}),1.0]])]});}
            var Q3;
            {var subQ0=sQuery(id+"F0.wireOp",EDGE,"E22.0.8.0");Q3=makeQuery(id+"F0.imprint","IMPRINT",FACE,{"disambiguationData":[TD([[makeQuery(id+"F0.imprint","IMPRINT",EDGE,{"derivedFrom":subQ0}),1.0]])]});}
            var Q4;
            {var subQ0=sQuery(id+"F0.wireOp",EDGE,"E22.0.7.0");Q4=makeQuery(id+"F0.imprint","IMPRINT",FACE,{"disambiguationData":[TD([[makeQuery(id+"F0.imprint","IMPRINT",EDGE,{"derivedFrom":subQ0}),1.0]])]});}
            var Q5;
            {var subQ0=sQuery(id+"F0.wireOp",EDGE,"E22.0.6.0");Q5=makeQuery(id+"F0.imprint","IMPRINT",FACE,{"disambiguationData":[TD([[makeQuery(id+"F0.imprint","IMPRINT",EDGE,{"derivedFrom":subQ0}),1.0]])]});}
            var Q6;
            {var subQ0=sQuery(id+"F0.wireOp",EDGE,"E22.0.5.0");Q6=makeQuery(id+"F0.imprint","IMPRINT",FACE,{"disambiguationData":[TD([[makeQuery(id+"F0.imprint","IMPRINT",EDGE,{"derivedFrom":subQ0}),1.0]])]});}
            var Q7;
            {var subQ1=sQuery(id+"F0.wireOp",EDGE,"E22.0.4.0");Q7=makeQuery(id+"F0.imprint","IMPRINT",FACE,{"disambiguationData":[TD([[makeQuery(id+"F0.imprint","IMPRINT",EDGE,{"derivedFrom":subQ1}),1.0]])]});}
            var Q8;
            {var subQ0=sQuery(id+"F0.wireOp",EDGE,"E22.0.3.0");Q8=makeQuery(id+"F0.imprint","IMPRINT",FACE,{"disambiguationData":[TD([[makeQuery(id+"F0.imprint","IMPRINT",EDGE,{"derivedFrom":subQ0}),1.0]])]});}
            var Q9;
            {var subQ0=sQuery(id+"F0.wireOp",EDGE,"E22.0.2.0");Q9=makeQuery(id+"F0.imprint","IMPRINT",FACE,{"disambiguationData":[TD([[makeQuery(id+"F0.imprint","IMPRINT",EDGE,{"derivedFrom":subQ0}),1.0]])]});}
            var Q10;
            {var subQ0=sQuery(id+"F0.wireOp",EDGE,"E22.0.1.0");Q10=makeQuery(id+"F0.imprint","IMPRINT",FACE,{"disambiguationData":[TD([[makeQuery(id+"F0.imprint","IMPRINT",EDGE,{"derivedFrom":subQ0}),1.0]])]});}
            var Q11;
            {var subQ0=sQuery(id+"F0.wireOp",EDGE,"E12");Q11=makeQuery(id+"F0.imprint","IMPRINT",FACE,{"disambiguationData":[TD([[makeQuery(id+"F0.imprint","IMPRINT",EDGE,{"derivedFrom":subQ0}),-1.0]])]});}
            var Q12;
            {var subQ1=sQuery(id+"F0.wireOp",EDGE,"E7");Q12=makeQuery(id+"F0.imprint","IMPRINT",FACE,{"disambiguationData":[TD([[makeQuery(id+"F0.imprint","IMPRINT",EDGE,{"derivedFrom":subQ1}),-1.0]])]});}
            extrude(context, id + "F1", {"entities" : qUnion([Q0, Q1, Q2, Q3, Q4, Q5, Q6, Q7, Q8, Q9, Q10, Q11, Q12]), "depth" : 2 * mm});
        }
    });
